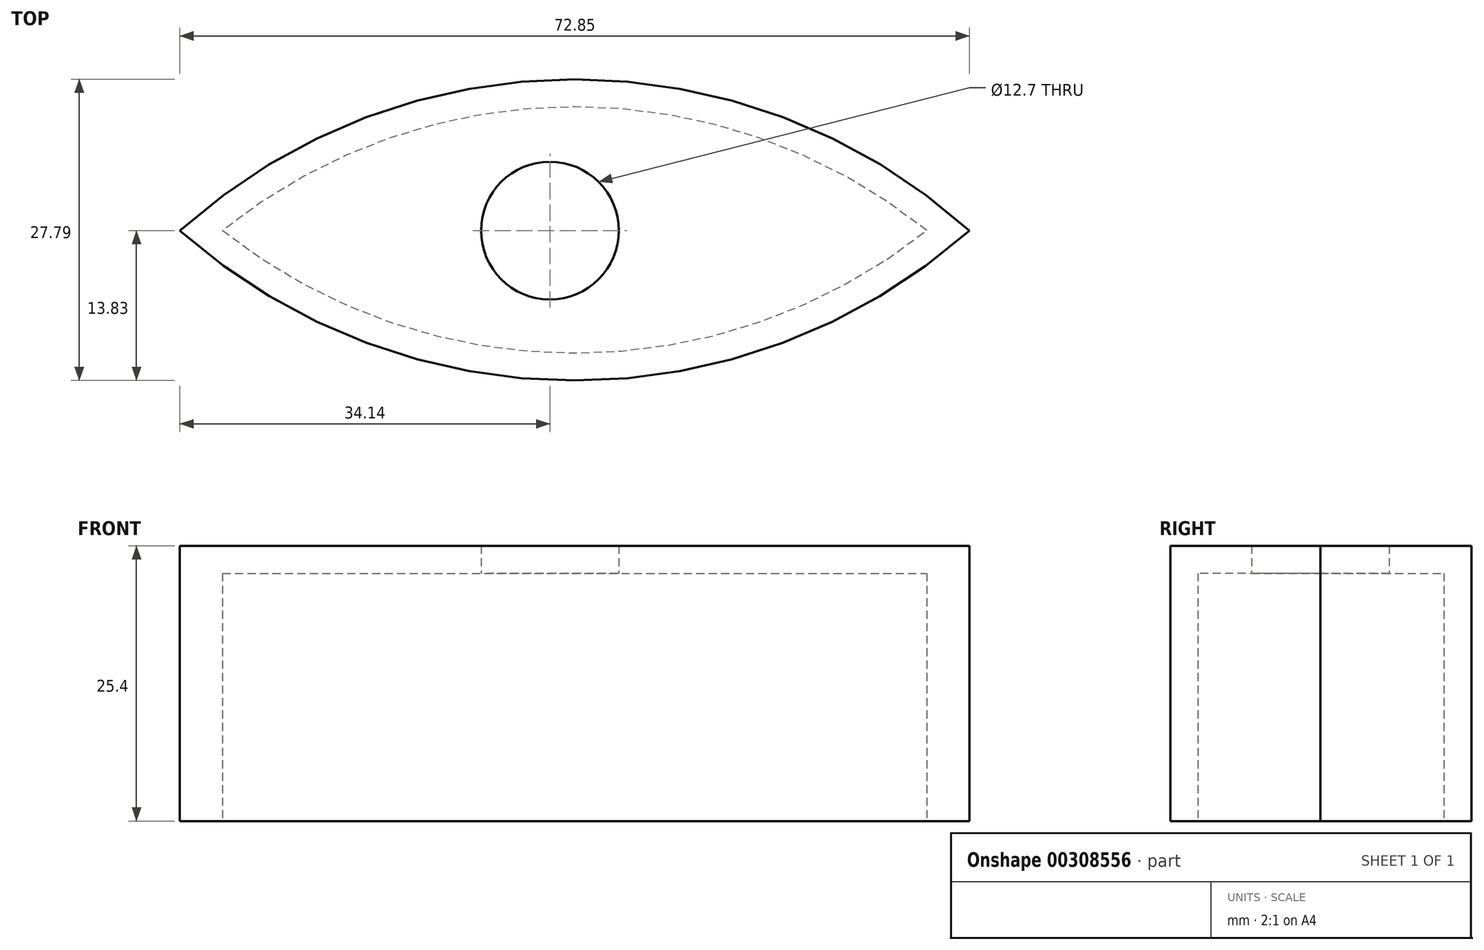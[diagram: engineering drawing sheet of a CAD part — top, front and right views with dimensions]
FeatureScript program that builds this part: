
annotation { "Feature Type Name" : "Feature", "Feature Type Description" : "" }
export const myFeature = defineFeature(function(context is Context, id is Id, definition is map)
    precondition{}
    {
        {
            var Q0;
            Q0=qCreatedBy(makeId("Top.planeOp"),FACE);
            var sketch = newSketch(context, id + "F0", { "sketchPlane" : qUnion([Q0])});
            skArc(sketch, "E0", {"start": v(38.7, 0) * mm, "mid": v(2.29, 13.96) * mm, "end": v(-34.14, 0) * mm});
            skArc(sketch, "E1", {"start": v(-34.14, 0) * mm, "mid": v(2.29, -13.83) * mm, "end": v(38.7, 0) * mm});
            skSolve(sketch);
        }
        {
            var Q0;
            Q0 = qSketchRegion(id + "F0", true);
            extrude(context, id + "F1", {"entities" : qUnion([Q0]), "depth" : 25.4 * mm});
        }
        {
            var Q0;
            Q0=makeQuery(id+"F1.opExtrude","CAP_FACE",FACE,{"disambiguationData":[OSD([sQuery(id+"F0.wireOp",EDGE,"E0"),sQuery(id+"F0.wireOp",EDGE,"E1")])],"isStart":true});
            shell(context, id + "F2", {"entities" : qUnion([Q0]), "thickness" : 2.54 * mm});
        }
        {
            var Q0;
            Q0=qCreatedBy(makeId("Top.planeOp"),FACE);
            var sketch = newSketch(context, id + "F3", { "sketchPlane" : qUnion([Q0])});
            skLineSegment(sketch, "E2", {"start": v(-34.14, 0) * mm, "end": v(38.7, 0) * mm});
            skLineSegment(sketch, "E3", {"start": v(0, 13.9) * mm, "end": v(0, -13.78) * mm});
            skPoint(sketch, "E4", {"position": v(0, 0) * mm});
            skSolve(sketch);
        }
        {
            var Q0;
            Q0=sQuery(id+"F3.wireOp",VERTEX,"E4");
            var Q1;
            Q1=makeQuery(id+"F1.opExtrude","SWEPT_BODY",BODY,{"disambiguationData":[OSD([sQuery(id+"F0.wireOp",EDGE,"E0"),sQuery(id+"F0.wireOp",EDGE,"E1")])]});
            hole(context, id + "F4", {"style" : HoleStyle.SIMPLE, "endStyle" : HoleEndStyle.THROUGH, "oppositeDirection" : true, "holeDiameter" : 12.7 * mm, "tappedDepth" : 12.7 * mm, "tapClearance" : 3, "locations" : qUnion([Q0]), "scope" : qUnion([Q1])});
        }
    });
